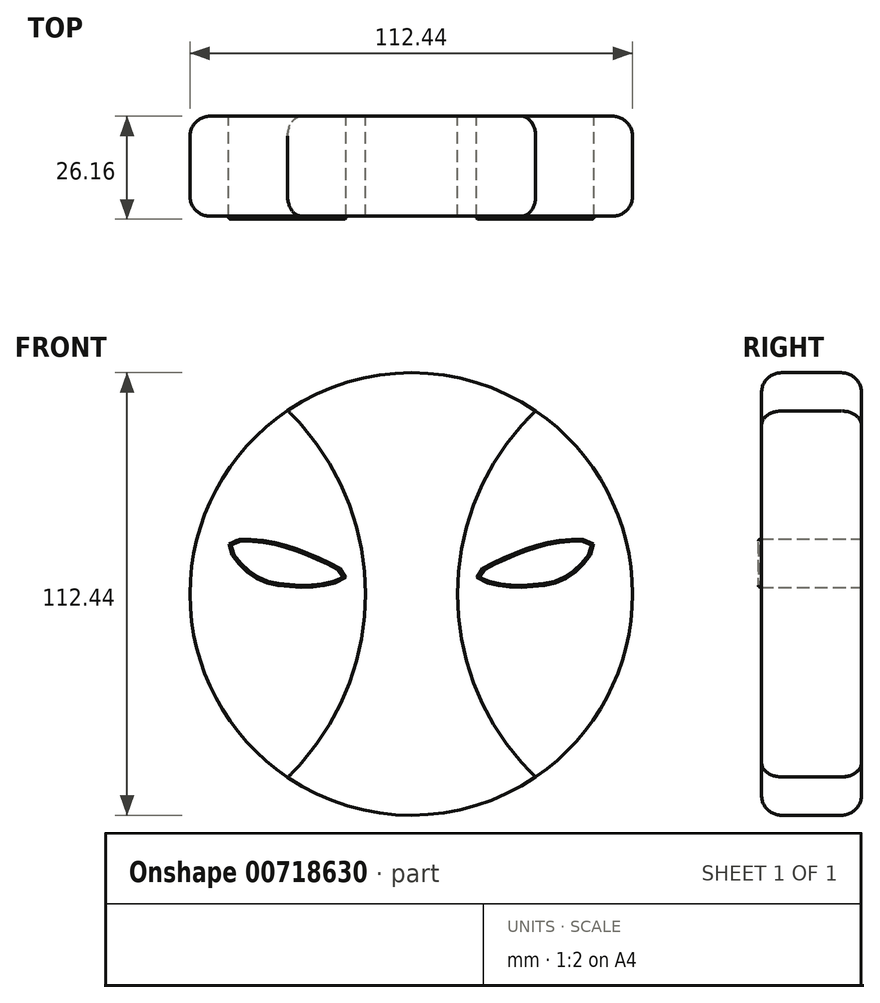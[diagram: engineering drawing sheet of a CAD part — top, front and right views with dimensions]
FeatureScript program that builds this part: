
annotation { "Feature Type Name" : "Feature", "Feature Type Description" : "" }
export const myFeature = defineFeature(function(context is Context, id is Id, definition is map)
    precondition{}
    {
        {
            var Q0;
            Q0=qCreatedBy(makeId("Front.planeOp"),FACE);
            var sketch = newSketch(context, id + "F0", { "sketchPlane" : qUnion([Q0])});
            skCircle(sketch, "E0", {"center": v(0, 0) * mm, "radius": 56.22 * mm});
            skLineSegment(sketch, "E1", {"start": v(0, 0) * mm, "end": v(11.43, 0) * mm});
            skLineSegment(sketch, "E2", {"start": v(0, 0) * mm, "end": v(-11.43, 0) * mm});
            skCircle(sketch, "E3", {"center": v(-76.3, 0) * mm, "radius": 64.7 * mm});
            skCircle(sketch, "E4", {"center": v(76.03, 0) * mm, "radius": 64.3 * mm});
            skSolve(sketch);
        }
        {
            var Q0;
            {var subQ0=sQuery(id+"F0.wireOp",EDGE,"E3");var subQ1=sQuery(id+"F0.wireOp",EDGE,"E0");var subQ2=makeQuery(id+"F0.imprint","INTERSECT",VERTEX,{"disambiguationData":[OD(0.0)],"derivedFrom":[subQ1,subQ0]});Q0=makeQuery(id+"F0.imprint","IMPRINT",FACE,{"disambiguationData":[TD([[makeQuery(id+"F0.imprint","IMPRINT",EDGE,{"disambiguationData":[TD([[subQ2,-1.0]])],"derivedFrom":subQ1}),1.0]])]});}
            var Q1;
            {var subQ0=sQuery(id+"F0.wireOp",EDGE,"E4");var subQ1=sQuery(id+"F0.wireOp",EDGE,"E0");var subQ2=makeQuery(id+"F0.imprint","INTERSECT",VERTEX,{"disambiguationData":[OD(0.0)],"derivedFrom":[subQ1,subQ0]});Q1=makeQuery(id+"F0.imprint","IMPRINT",FACE,{"disambiguationData":[TD([[makeQuery(id+"F0.imprint","IMPRINT",EDGE,{"disambiguationData":[TD([[subQ2,1.0]])],"derivedFrom":subQ1}),1.0]])]});}
            extrude(context, id + "F1", {"entities" : qUnion([Q0, Q1]), "depth" : 25.4 * mm, "offsetDistance" : 25.4 * mm});
        }
        {
            var Q0;
            {var subQ0=sQuery(id+"F0.wireOp",EDGE,"E3");var subQ1=sQuery(id+"F0.wireOp",EDGE,"E0");var subQ2=makeQuery(id+"F0.imprint","INTERSECT",VERTEX,{"disambiguationData":[OD(0.0)],"derivedFrom":[subQ1,subQ0]});Q0=makeQuery(id+"F0.imprint","IMPRINT",FACE,{"disambiguationData":[TD([[makeQuery(id+"F0.imprint","IMPRINT",EDGE,{"disambiguationData":[TD([[subQ2,1.0]])],"derivedFrom":subQ1}),1.0]])]});}
            extrude(context, id + "F2", {"entities" : qUnion([Q0]), "depth" : 25.4 * mm, "offsetDistance" : 25.4 * mm});
        }
        {
            var Q0;
            {var subQ0=sQuery(id+"F0.wireOp",EDGE,"E0");Q0=makeQuery(id+"F2.opExtrude","CAP_EDGE",EDGE,{"disambiguationData":[OSD([subQ0]),TDD([makeQuery(id+"F0.imprint","IMPRINT",EDGE,{"disambiguationData":[TD([[makeQuery(id+"F0.imprint","INTERSECT",VERTEX,{"disambiguationData":[OD(0.0)],"derivedFrom":[subQ0,sQuery(id+"F0.wireOp",EDGE,"E3")]}),1.0]])],"derivedFrom":subQ0})])],"isStart":false});}
            var Q1;
            {var subQ0=sQuery(id+"F0.wireOp",EDGE,"E4");var subQ1=sQuery(id+"F0.wireOp",EDGE,"E0");Q1=makeQuery(id+"F1.opExtrude","CAP_EDGE",EDGE,{"disambiguationData":[OSD([subQ1]),TDD([makeQuery(id+"F0.imprint","IMPRINT",EDGE,{"disambiguationData":[TD([[makeQuery(id+"F0.imprint","INTERSECT",VERTEX,{"disambiguationData":[OD(0.0)],"derivedFrom":[subQ1,subQ0]}),1.0]])],"derivedFrom":subQ1})])],"isStart":false});}
            var Q2;
            {var subQ0=sQuery(id+"F0.wireOp",EDGE,"E3");var subQ1=sQuery(id+"F0.wireOp",EDGE,"E0");Q2=makeQuery(id+"F1.opExtrude","CAP_EDGE",EDGE,{"disambiguationData":[OSD([subQ1]),TDD([makeQuery(id+"F0.imprint","IMPRINT",EDGE,{"disambiguationData":[TD([[makeQuery(id+"F0.imprint","INTERSECT",VERTEX,{"disambiguationData":[OD(0.0)],"derivedFrom":[subQ1,subQ0]}),-1.0]])],"derivedFrom":subQ1})])],"isStart":false});}
            var Q3;
            {var subQ0=sQuery(id+"F0.wireOp",EDGE,"E0");Q3=makeQuery(id+"F2.opExtrude","CAP_EDGE",EDGE,{"disambiguationData":[OSD([subQ0]),TDD([makeQuery(id+"F0.imprint","IMPRINT",EDGE,{"disambiguationData":[TD([[makeQuery(id+"F0.imprint","INTERSECT",VERTEX,{"disambiguationData":[OD(1.0)],"derivedFrom":[subQ0,sQuery(id+"F0.wireOp",EDGE,"E3")]}),-1.0]])],"derivedFrom":subQ0})])],"isStart":false});}
            var Q4;
            {var subQ0=sQuery(id+"F0.wireOp",EDGE,"E0");Q4=makeQuery(id+"F2.opExtrude","CAP_EDGE",EDGE,{"disambiguationData":[OSD([subQ0]),TDD([makeQuery(id+"F0.imprint","IMPRINT",EDGE,{"disambiguationData":[TD([[makeQuery(id+"F0.imprint","INTERSECT",VERTEX,{"disambiguationData":[OD(0.0)],"derivedFrom":[subQ0,sQuery(id+"F0.wireOp",EDGE,"E3")]}),1.0]])],"derivedFrom":subQ0})])],"isStart":true});}
            var Q5;
            {var subQ0=sQuery(id+"F0.wireOp",EDGE,"E4");var subQ1=sQuery(id+"F0.wireOp",EDGE,"E0");Q5=makeQuery(id+"F1.opExtrude","CAP_EDGE",EDGE,{"disambiguationData":[OSD([subQ1]),TDD([makeQuery(id+"F0.imprint","IMPRINT",EDGE,{"disambiguationData":[TD([[makeQuery(id+"F0.imprint","INTERSECT",VERTEX,{"disambiguationData":[OD(0.0)],"derivedFrom":[subQ1,subQ0]}),1.0]])],"derivedFrom":subQ1})])],"isStart":true});}
            var Q6;
            {var subQ0=sQuery(id+"F0.wireOp",EDGE,"E0");Q6=makeQuery(id+"F2.opExtrude","CAP_EDGE",EDGE,{"disambiguationData":[OSD([subQ0]),TDD([makeQuery(id+"F0.imprint","IMPRINT",EDGE,{"disambiguationData":[TD([[makeQuery(id+"F0.imprint","INTERSECT",VERTEX,{"disambiguationData":[OD(1.0)],"derivedFrom":[subQ0,sQuery(id+"F0.wireOp",EDGE,"E3")]}),-1.0]])],"derivedFrom":subQ0})])],"isStart":true});}
            var Q7;
            {var subQ0=sQuery(id+"F0.wireOp",EDGE,"E3");var subQ1=sQuery(id+"F0.wireOp",EDGE,"E0");Q7=makeQuery(id+"F1.opExtrude","CAP_EDGE",EDGE,{"disambiguationData":[OSD([subQ1]),TDD([makeQuery(id+"F0.imprint","IMPRINT",EDGE,{"disambiguationData":[TD([[makeQuery(id+"F0.imprint","INTERSECT",VERTEX,{"disambiguationData":[OD(0.0)],"derivedFrom":[subQ1,subQ0]}),-1.0]])],"derivedFrom":subQ1})])],"isStart":true});}
            fillet(context, id + "F3", {"entities" : qUnion([Q0, Q1, Q2, Q3, Q4, Q5, Q6, Q7]), "radius" : 5.08 * mm, "tangentPropagation" : true, "allowEdgeOverflow" : false});
        }
        {
            var Q0;
            Q0=qCreatedBy(makeId("Front.planeOp"),FACE);
            var sketch = newSketch(context, id + "F4", { "sketchPlane" : qUnion([Q0])});
            skFitSpline(sketch, "E5", {"points": [v(-46.3, 17.78) * mm, v(-40.2, 9.55) * mm, v(-32.77, 7.16) * mm, v(-24.55, 6.9) * mm, v(-16.59, 9.55) * mm, v(-21.9, 13.53) * mm, v(-31.98, 17.51) * mm, v(-39.14, 18.84) * mm, v(-46.3, 17.78) * mm]});
            skSolve(sketch);
        }
        {
            var Q0;
            Q0 = qSketchRegion(id + "F4", true);
            extrude(context, id + "F5", {"entities" : qUnion([Q0]), "depth" : 26.16 * mm, "offsetDistance" : 25.4 * mm});
        }
        {
            var Q0;
            Q0=makeQuery(id+"F5.opExtrude","CAP_EDGE",EDGE,{"disambiguationData":[OSD([sQuery(id+"F4.wireOp",EDGE,"E5")])],"isStart":false});
            var Q1;
            Q1=makeQuery(id+"FxjCx0XTqow1Etq_3.opPattern","COPY",EDGE,{"derivedFrom":makeQuery(id+"F5.opExtrude","CAP_EDGE",EDGE,{"disambiguationData":[OSD([sQuery(id+"F4.wireOp",EDGE,"E5")])],"isStart":false}),"instanceName":"1"});
            fillet(context, id + "F6", {"entities" : qUnion([Q0, Q1]), "radius" : 0.5 * mm, "tangentPropagation" : true, "allowEdgeOverflow" : false});
        }
        {
            var Q0;
            Q0=makeQuery(id+"F5.opExtrude","SWEPT_BODY",BODY,{"disambiguationData":[OSD([sQuery(id+"F4.wireOp",EDGE,"E5")])]});
            transform(context, id + "F7", {"entities" : qUnion([Q0]), "transformType" : TransformType.TRANSLATION_3D, "dx" : 0 * mm, "dy" : 0 * mm, "dz" : -5.08 * mm, "makeCopy" : false});
        }
        {
            var Q0;
            Q0=makeQuery(id+"F5.opExtrude","SWEPT_BODY",BODY,{"disambiguationData":[OSD([sQuery(id+"F4.wireOp",EDGE,"E5")])]});
            var Q1;
            Q1=qCreatedBy(makeId("Right.planeOp"),FACE);
            mirror(context, id + "F8", {"entities" : qUnion([Q0]), "mirrorPlane" : qUnion([Q1])});
        }
    });
